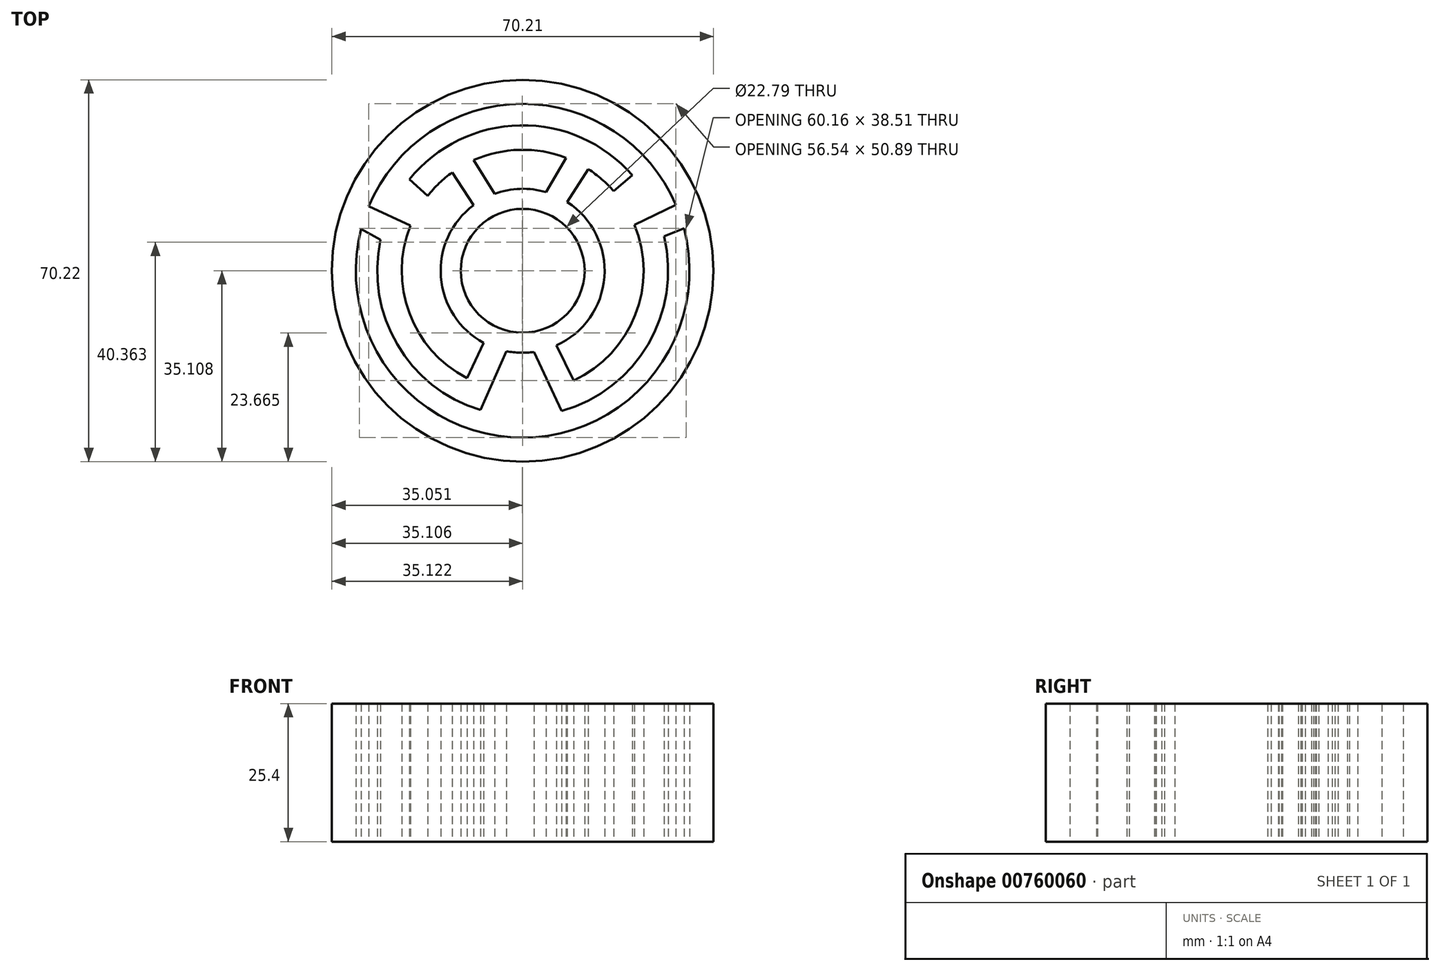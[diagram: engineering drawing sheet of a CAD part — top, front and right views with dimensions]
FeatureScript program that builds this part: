
annotation { "Feature Type Name" : "Feature", "Feature Type Description" : "" }
export const myFeature = defineFeature(function(context is Context, id is Id, definition is map)
    precondition{}
    {
        {
            var Q0;
            Q0=qCreatedBy(makeId("Top.planeOp"),FACE);
            var sketch = newSketch(context, id + "F0", { "sketchPlane" : qUnion([Q0])});
            skCircle(sketch, "E0", {"center": v(37.46, 38.19) * mm, "radius": 35.1 * mm});
            skArc(sketch, "E1", {"start": v(7.73, 45.85) * mm, "mid": v(37.53, 7.49) * mm, "end": v(67.15, 46) * mm});
            skArc(sketch, "E2", {"start": v(43.65, 24.44) * mm, "mid": v(52.5, 37.04) * mm, "end": v(45.66, 50.84) * mm});
            skCircle(sketch, "E3", {"center": v(37.46, 38.19) * mm, "radius": 11.4 * mm});
            skArc(sketch, "E4", {"start": v(16.8, 46.47) * mm, "mid": v(16.6, 30.44) * mm, "end": v(27.22, 18.43) * mm});
            skArc(sketch, "E5", {"start": v(11.31, 43.92) * mm, "mid": v(14.37, 24.64) * mm, "end": v(29.71, 12.57) * mm});
            skLineSegment(sketch, "E6", {"start": v(32.3, 52.36) * mm, "end": v(28.45, 58.54) * mm});
            skLineSegment(sketch, "E7", {"start": v(28.4, 50.25) * mm, "end": v(24.49, 56.28) * mm});
            skLineSegment(sketch, "E8", {"start": v(41.77, 52.64) * mm, "end": v(45.46, 58.96) * mm});
            skLineSegment(sketch, "E9", {"start": v(45.66, 50.84) * mm, "end": v(49.54, 56.88) * mm});
            skLineSegment(sketch, "E10", {"start": v(54.21, 52.84) * mm, "end": v(57.64, 55.76) * mm});
            skLineSegment(sketch, "E11", {"start": v(58.05, 46.64) * mm, "end": v(65.67, 50.29) * mm});
            skLineSegment(sketch, "E12", {"start": v(19.98, 51.97) * mm, "end": v(16.63, 55) * mm});
            skLineSegment(sketch, "E13", {"start": v(16.8, 46.47) * mm, "end": v(9.13, 50.03) * mm});
            skLineSegment(sketch, "E14", {"start": v(30.28, 24.92) * mm, "end": v(27.22, 18.43) * mm});
            skLineSegment(sketch, "E15", {"start": v(43.65, 24.44) * mm, "end": v(46.82, 18) * mm});
            skLineSegment(sketch, "E16", {"start": v(39.55, 23.25) * mm, "end": v(44.62, 12.4) * mm});
            skLineSegment(sketch, "E17", {"start": v(34.47, 23.4) * mm, "end": v(29.71, 12.57) * mm});
            skLineSegment(sketch, "E18", {"start": v(63.46, 44.52) * mm, "end": v(67.15, 46) * mm});
            skLineSegment(sketch, "E19", {"start": v(11.31, 43.92) * mm, "end": v(7.73, 45.85) * mm});
            skArc(sketch, "E20.trimOffspring", {"start": v(46.82, 18) * mm, "mid": v(58.18, 30.07) * mm, "end": v(58.05, 46.64) * mm});
            skArc(sketch, "E21.trimOffspring", {"start": v(44.62, 12.4) * mm, "mid": v(60.54, 24.65) * mm, "end": v(63.46, 44.52) * mm});
            skArc(sketch, "E22.trimOffspring", {"start": v(57.64, 55.76) * mm, "mid": v(36.96, 64.95) * mm, "end": v(16.63, 55) * mm});
            skArc(sketch, "E23.trimOffspring", {"start": v(65.67, 50.29) * mm, "mid": v(37.31, 68.89) * mm, "end": v(9.13, 50.03) * mm});
            skArc(sketch, "E24.trimOffspring", {"start": v(54.21, 52.84) * mm, "mid": v(52.02, 55.02) * mm, "end": v(49.54, 56.88) * mm});
            skArc(sketch, "E25.trimOffspring", {"start": v(34.47, 23.4) * mm, "mid": v(37, 23.11) * mm, "end": v(39.55, 23.25) * mm});
            skArc(sketch, "E26.trimOffspring", {"start": v(28.4, 50.25) * mm, "mid": v(22.42, 37.07) * mm, "end": v(30.28, 24.92) * mm});
            skArc(sketch, "E27.trimOffspring", {"start": v(41.77, 52.64) * mm, "mid": v(37.02, 53.26) * mm, "end": v(32.3, 52.36) * mm});
            skArc(sketch, "E28.trimOffspring", {"start": v(45.46, 58.96) * mm, "mid": v(36.91, 60.44) * mm, "end": v(28.45, 58.54) * mm});
            skArc(sketch, "E29.trimOffspring", {"start": v(24.49, 56.28) * mm, "mid": v(22.08, 54.28) * mm, "end": v(19.98, 51.97) * mm});
            skSolve(sketch);
        }
        {
            var Q0;
            Q0=makeQuery(id+"F0.imprint","IMPRINT",FACE,{"disambiguationData":[TD([[makeQuery(id+"F0.imprint","IMPRINT",EDGE,{"derivedFrom":sQuery(id+"F0.wireOp",EDGE,"E0")}),1.0]])]});
            extrude(context, id + "F1", {"entities" : qUnion([Q0]), "depth" : 25.4 * mm, "offsetDistance" : 25.4 * mm});
        }
    });
